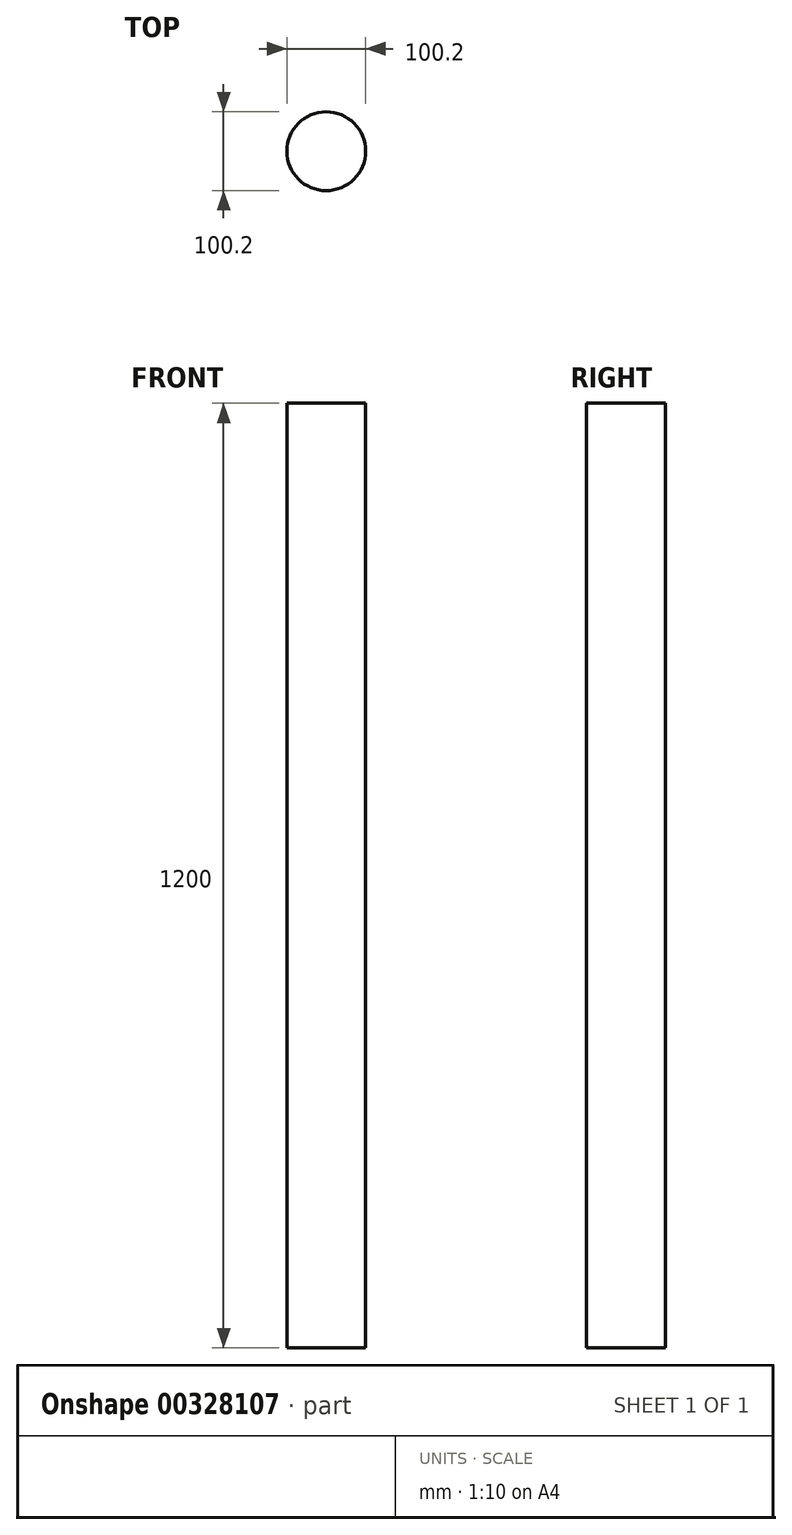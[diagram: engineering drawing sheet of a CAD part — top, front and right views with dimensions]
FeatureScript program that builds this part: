
annotation { "Feature Type Name" : "Feature", "Feature Type Description" : "" }
export const myFeature = defineFeature(function(context is Context, id is Id, definition is map)
    precondition{}
    {
        {
            var Q0;
            Q0=qCreatedBy(makeId("Top.planeOp"),FACE);
            var sketch = newSketch(context, id + "F0", { "sketchPlane" : qUnion([Q0])});
            skCircle(sketch, "E0", {"center": v(0, 0) * mm, "radius": 50.1 * mm});
            skSolve(sketch);
        }
        {
            var Q0;
            Q0=sQuery(id+"F0.wireOp",EDGE,"E0");
            extrude(context, id + "F1", {"bodyType" : ExtendedToolBodyType.SURFACE, "surfaceEntities" : qUnion([Q0]), "depth" : 1200 * mm});
        }
    });
